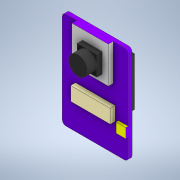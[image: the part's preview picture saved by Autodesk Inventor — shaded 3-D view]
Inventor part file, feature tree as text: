
AUTODESK INVENTOR PART (.ipt)
format: ipt  version: 2020 (Build 240168000, 168)  size: 202,240 bytes
history: native  units: mm
features: extrude x7, sketch x5
ambient origin geometry x8: Origin, YZ Plane, XZ Plane, XY Plane, X Axis, Y Axis, Z Axis, Center Point
bodies: Solid1 (feature_tree)
feature tree (12):
  extrude  "Extrusion1"  Depth=27.17mm
  sketch  "Sketch2"  dims[d2=1.5mm d3=1.6mm d4=0.0mm]
  extrude  "Extrusion2"  Depth=1.6mm TaperAngle=0.0deg
  extrude  "Extrusion3"  Depth=15.0mm
  extrude  "Extrusion4"  Depth=5.7mm
  extrude  "Extrusion5"  Depth=5.5mm
  extrude  "Extrusion6"  Depth=11.8mm
  extrude  "Extrusion7"  Depth=4.0mm
  sketch  "Sketch1"  dims[d0=40.0mm d1=27.17mm]
  sketch  "Sketch3"  dims[d5=15.0mm d6=15.0mm]
  sketch  "Sketch4"  dims[d7=6.0mm d8=5.7mm]
  sketch  "Sketch5"  dims[d9=16.3mm d10=5.5mm d11=11.8mm d12=4.0mm d13=4.0mm d14=8.8mm d15=2.0mm d16=0.0mm d17=2.0mm d18=0.0mm d19=1.0mm d20=0.0mm d21=8.1mm d22=8.1mm d23=3.9mm d24=8.7mm d25=2.2mm d26=0.0mm d27=7.8mm d28=3.7mm d29=0.0mm d30=25.1mm d31=2.0mm d32=1.035mm d33=1.035mm d36=3.6mm d37=2.0mm d38=0.0mm d39=20.0mm]
